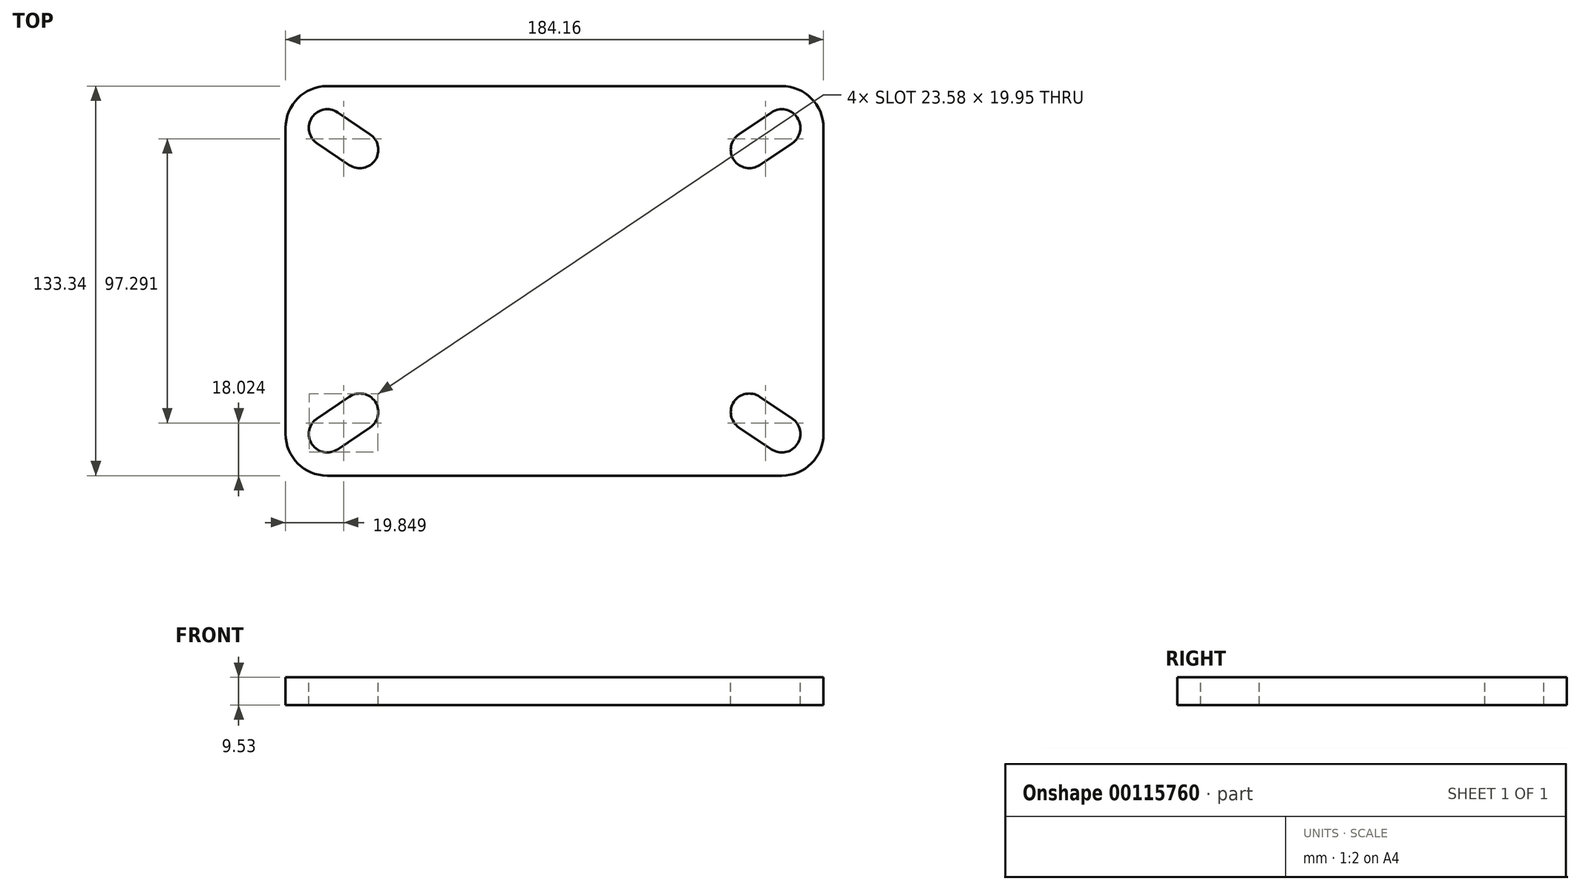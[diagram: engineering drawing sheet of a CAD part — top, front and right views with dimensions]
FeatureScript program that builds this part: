
annotation { "Feature Type Name" : "Feature", "Feature Type Description" : "" }
export const myFeature = defineFeature(function(context is Context, id is Id, definition is map)
    precondition{}
    {
        {
            var Q0;
            Q0=qCreatedBy(makeId("Top.planeOp"),FACE);
            var sketch = newSketch(context, id + "F0", { "sketchPlane" : qUnion([Q0])});
            skLineSegment(sketch, "E0.bottom", {"start": v(77.79, -66.68) * mm, "end": v(-77.79, -66.68) * mm});
            skLineSegment(sketch, "E0.top", {"start": v(77.79, 66.68) * mm, "end": v(-77.79, 66.68) * mm});
            skLineSegment(sketch, "E0.left", {"start": v(92.08, -52.39) * mm, "end": v(92.08, 52.39) * mm});
            skLineSegment(sketch, "E0.right", {"start": v(-92.08, -52.39) * mm, "end": v(-92.08, 52.39) * mm});
            skPoint(sketch, "E0.middle", {"position": v(0, 0) * mm});
            skArc(sketch, "E1", {"start": v(-77.79, 66.68) * mm, "mid": v(-87.9, 62.5) * mm, "end": v(-92.08, 52.39) * mm});
            skArc(sketch, "E2", {"start": v(92.07, 52.39) * mm, "mid": v(87.9, 62.5) * mm, "end": v(77.79, 66.68) * mm});
            skArc(sketch, "E3", {"start": v(-92.07, -52.39) * mm, "mid": v(-87.9, -62.5) * mm, "end": v(-77.79, -66.67) * mm});
            skArc(sketch, "E4", {"start": v(77.79, -66.67) * mm, "mid": v(87.9, -62.5) * mm, "end": v(92.08, -52.39) * mm});
            skPoint(sketch, "E5.orphan", {"position": v(92.08, 66.68) * mm});
            skPoint(sketch, "E6.orphan", {"position": v(92.08, -66.68) * mm});
            skPoint(sketch, "E7.orphan", {"position": v(-92.08, -66.68) * mm});
            skPoint(sketch, "E8.orphan", {"position": v(-92.08, 66.68) * mm});
            skArc(sketch, "E9", {"start": v(-74.24, 57.65) * mm, "mid": v(-83.05, 55.93) * mm, "end": v(-81.33, 47.12) * mm});
            skArc(sketch, "E10", {"start": v(81.33, 47.12) * mm, "mid": v(83.05, 55.93) * mm, "end": v(74.24, 57.65) * mm});
            skArc(sketch, "E11", {"start": v(74.24, -57.65) * mm, "mid": v(83.05, -55.93) * mm, "end": v(81.33, -47.12) * mm});
            skArc(sketch, "E12", {"start": v(-81.33, -47.12) * mm, "mid": v(-83.05, -55.93) * mm, "end": v(-74.24, -57.65) * mm});
            skArc(sketch, "E13", {"start": v(-70.22, 39.64) * mm, "mid": v(-61.4, 41.36) * mm, "end": v(-63.13, 50.17) * mm});
            skArc(sketch, "E14", {"start": v(63.13, 50.17) * mm, "mid": v(61.4, 41.36) * mm, "end": v(70.22, 39.64) * mm});
            skArc(sketch, "E15", {"start": v(-63.13, -50.17) * mm, "mid": v(-61.4, -41.36) * mm, "end": v(-70.22, -39.64) * mm});
            skArc(sketch, "E16", {"start": v(70.22, -39.64) * mm, "mid": v(61.4, -41.36) * mm, "end": v(63.13, -50.17) * mm});
            skLineSegment(sketch, "E17", {"start": v(-74.24, 57.65) * mm, "end": v(-63.13, 50.17) * mm});
            skLineSegment(sketch, "E18", {"start": v(-81.33, 47.12) * mm, "end": v(-70.22, 39.64) * mm});
            skLineSegment(sketch, "E19", {"start": v(63.13, 50.17) * mm, "end": v(74.24, 57.65) * mm});
            skLineSegment(sketch, "E20", {"start": v(70.22, 39.64) * mm, "end": v(81.33, 47.12) * mm});
            skLineSegment(sketch, "E21", {"start": v(70.22, -39.64) * mm, "end": v(81.33, -47.12) * mm});
            skLineSegment(sketch, "E22", {"start": v(63.13, -50.17) * mm, "end": v(74.24, -57.65) * mm});
            skLineSegment(sketch, "E23", {"start": v(-74.24, -57.65) * mm, "end": v(-63.13, -50.17) * mm});
            skLineSegment(sketch, "E24", {"start": v(-81.33, -47.12) * mm, "end": v(-70.22, -39.64) * mm});
            skSolve(sketch);
        }
        {
            var Q0;
            Q0 = qSketchRegion(id + "F0", true);
            extrude(context, id + "F1", {"entities" : qUnion([Q0]), "oppositeDirection" : true, "depth" : 9.52 * mm});
        }
    });
